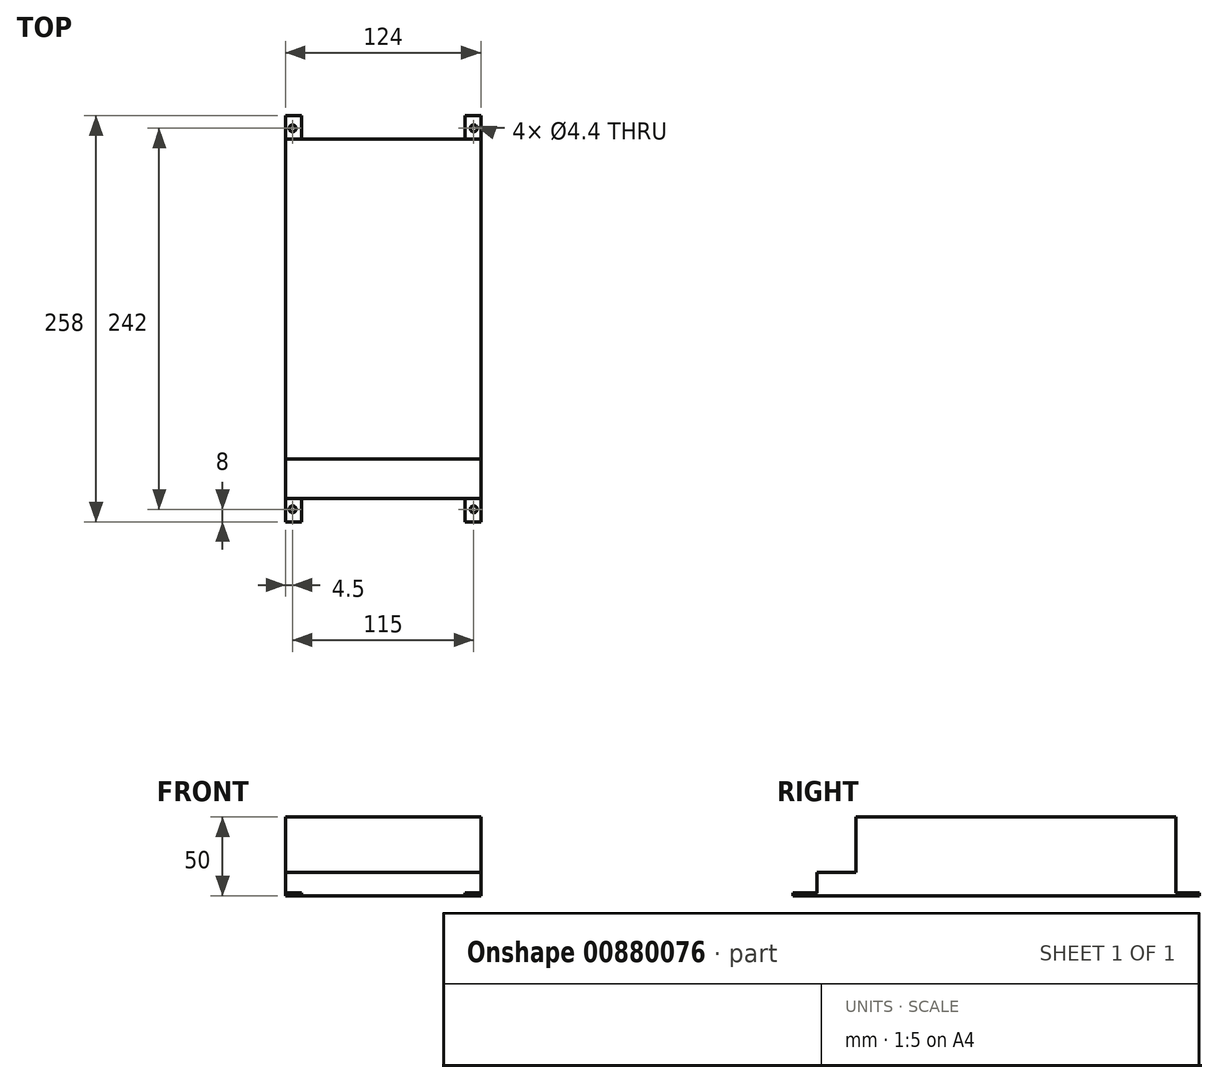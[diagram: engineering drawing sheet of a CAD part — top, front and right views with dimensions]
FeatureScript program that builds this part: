
annotation { "Feature Type Name" : "Feature", "Feature Type Description" : "" }
export const myFeature = defineFeature(function(context is Context, id is Id, definition is map)
    precondition{}
    {
        {
            var Q0;
            Q0=qCreatedBy(makeId("Top.planeOp"),FACE);
            var sketch = newSketch(context, id + "F0", { "sketchPlane" : qUnion([Q0])});
            skLineSegment(sketch, "E0.bottom", {"start": v(62, -114) * mm, "end": v(-62, -114) * mm});
            skLineSegment(sketch, "E0.top", {"start": v(62, 114) * mm, "end": v(-62, 114) * mm});
            skLineSegment(sketch, "E0.left", {"start": v(62, -114) * mm, "end": v(62, 114) * mm});
            skLineSegment(sketch, "E0.right", {"start": v(-62, -114) * mm, "end": v(-62, 114) * mm});
            skPoint(sketch, "E0.middle", {"position": v(0, 0) * mm});
            skSolve(sketch);
        }
        {
            var Q0;
            Q0=makeQuery(id+"F0.imprint","IMPRINT",FACE,{"disambiguationData":[TD([[makeQuery(id+"F0.imprint","IMPRINT",EDGE,{"derivedFrom":sQuery(id+"F0.wireOp",EDGE,"E0.bottom")}),-1.0]])]});
            extrude(context, id + "F1", {"entities" : qUnion([Q0]), "depth" : 15 * mm});
        }
        {
            var Q0;
            Q0=makeQuery(id+"F1.opExtrude","CAP_FACE",FACE,{"disambiguationData":[OSD([sQuery(id+"F0.wireOp",EDGE,"E0.bottom"),sQuery(id+"F0.wireOp",EDGE,"E0.top"),sQuery(id+"F0.wireOp",EDGE,"E0.left"),sQuery(id+"F0.wireOp",EDGE,"E0.right")])],"isStart":false});
            var sketch = newSketch(context, id + "F2", { "sketchPlane" : qUnion([Q0])});
            skLineSegment(sketch, "E1.bottom", {"start": v(-62, 114) * mm, "end": v(62, 114) * mm});
            skLineSegment(sketch, "E1.top", {"start": v(-62, -89) * mm, "end": v(62, -89) * mm});
            skLineSegment(sketch, "E1.left", {"start": v(-62, 114) * mm, "end": v(-62, -89) * mm});
            skLineSegment(sketch, "E1.right", {"start": v(62, 114) * mm, "end": v(62, -89) * mm});
            skSolve(sketch);
        }
        {
            var Q0;
            Q0=qSketchRegion(id+"F2",true);
            extrude(context, id + "F3", {"entities" : qUnion([Q0]), "operationType" : NewBodyOperationType.ADD, "depth" : 35 * mm});
        }
        {
            var Q0;
            Q0=makeQuery(id+"F1.opExtrude","CAP_FACE",FACE,{"disambiguationData":[OSD([sQuery(id+"F0.wireOp",EDGE,"E0.bottom"),sQuery(id+"F0.wireOp",EDGE,"E0.top"),sQuery(id+"F0.wireOp",EDGE,"E0.left"),sQuery(id+"F0.wireOp",EDGE,"E0.right")])],"isStart":true});
            var sketch = newSketch(context, id + "F4", { "sketchPlane" : qUnion([Q0])});
            skLineSegment(sketch, "E2.bottom", {"start": v(57.5, -121) * mm, "end": v(-57.5, -121) * mm, "construction": true});
            skLineSegment(sketch, "E2.top", {"start": v(57.5, 121) * mm, "end": v(-57.5, 121) * mm, "construction": true});
            skLineSegment(sketch, "E2.left", {"start": v(57.5, -121) * mm, "end": v(57.5, 121) * mm, "construction": true});
            skLineSegment(sketch, "E2.right", {"start": v(-57.5, -121) * mm, "end": v(-57.5, 121) * mm, "construction": true});
            skLineSegment(sketch, "E3", {"start": v(57.5, -121) * mm, "end": v(-57.5, 121) * mm, "construction": true});
            skPoint(sketch, "E4", {"position": v(0, 0) * mm});
            skSolve(sketch);
        }
        {
            var Q0;
            Q0=makeQuery(id+"F4.imprint","IMPRINT",FACE,{"disambiguationData":[TD([[makeQuery(id+"F4.imprint","IMPRINT",EDGE,{"derivedFrom":makeQuery(id+"F1.opExtrude","CAP_EDGE",EDGE,{"disambiguationData":[OSD([sQuery(id+"F0.wireOp",EDGE,"E0.bottom")])],"isStart":true})}),1.0]])]});
            var sketch = newSketch(context, id + "F5", { "sketchPlane" : qUnion([Q0])});
            skLineSegment(sketch, "E5.bottom", {"start": v(-62, 114) * mm, "end": v(-52, 114) * mm});
            skLineSegment(sketch, "E5.top", {"start": v(-62, 129) * mm, "end": v(-52, 129) * mm});
            skLineSegment(sketch, "E5.left", {"start": v(-62, 114) * mm, "end": v(-62, 129) * mm});
            skLineSegment(sketch, "E5.right", {"start": v(-52, 114) * mm, "end": v(-52, 129) * mm});
            skLineSegment(sketch, "E6.bottom", {"start": v(62, 114) * mm, "end": v(52, 114) * mm});
            skLineSegment(sketch, "E6.top", {"start": v(62, 129) * mm, "end": v(52, 129) * mm});
            skLineSegment(sketch, "E6.left", {"start": v(62, 114) * mm, "end": v(62, 129) * mm});
            skLineSegment(sketch, "E6.right", {"start": v(52, 114) * mm, "end": v(52, 129) * mm});
            skLineSegment(sketch, "E7.bottom", {"start": v(62, -114) * mm, "end": v(52, -114) * mm});
            skLineSegment(sketch, "E7.top", {"start": v(62, -129) * mm, "end": v(52, -129) * mm});
            skLineSegment(sketch, "E7.left", {"start": v(62, -114) * mm, "end": v(62, -129) * mm});
            skLineSegment(sketch, "E7.right", {"start": v(52, -114) * mm, "end": v(52, -129) * mm});
            skLineSegment(sketch, "E8.bottom", {"start": v(-62, -114) * mm, "end": v(-52, -114) * mm});
            skLineSegment(sketch, "E8.top", {"start": v(-62, -129) * mm, "end": v(-52, -129) * mm});
            skLineSegment(sketch, "E8.left", {"start": v(-62, -114) * mm, "end": v(-62, -129) * mm});
            skLineSegment(sketch, "E8.right", {"start": v(-52, -114) * mm, "end": v(-52, -129) * mm});
            skSolve(sketch);
        }
        {
            var Q0;
            Q0=qSketchRegion(id+"F5",true);
            extrude(context, id + "F6", {"entities" : qUnion([Q0]), "operationType" : NewBodyOperationType.ADD, "oppositeDirection" : true, "depth" : 2 * mm});
        }
        {
            var Q0;
            Q0=sQuery(id+"F4.wireOp",VERTEX,"E3.start");
            var Q1;
            Q1=sQuery(id+"F4.wireOp",VERTEX,"E2.right.start");
            var Q2;
            Q2=sQuery(id+"F4.wireOp",VERTEX,"E3.end");
            var Q3;
            Q3=sQuery(id+"F4.wireOp",VERTEX,"E2.left.end");
            var Q4;
            Q4=makeQuery(id+"F1.opExtrude","SWEPT_BODY",BODY,{"disambiguationData":[OSD([sQuery(id+"F0.wireOp",EDGE,"E0.bottom"),sQuery(id+"F0.wireOp",EDGE,"E0.top"),sQuery(id+"F0.wireOp",EDGE,"E0.left"),sQuery(id+"F0.wireOp",EDGE,"E0.right")])]});
            hole(context, id + "F7", {"style" : HoleStyle.SIMPLE, "endStyle" : HoleEndStyle.THROUGH, "standardTappedOrClearance" : lookupTablePath({ "standard" : "ISO", "fit" : "Normal", "size" : "M4", "type" : "Clearance" }), "standardBlindInLast" : lookupTablePath({ "fit" : "Standard", "standard" : "ISO", "size" : "M4", "type" : "Clearance" }), "holeDiameter" : 4.4 * mm, "isTappedThrough" : true, "tappedDepth" : 12 * mm, "tapClearance" : 3, "locations" : qUnion([Q0, Q1, Q2, Q3]), "scope" : qUnion([Q4])});
        }
    });
